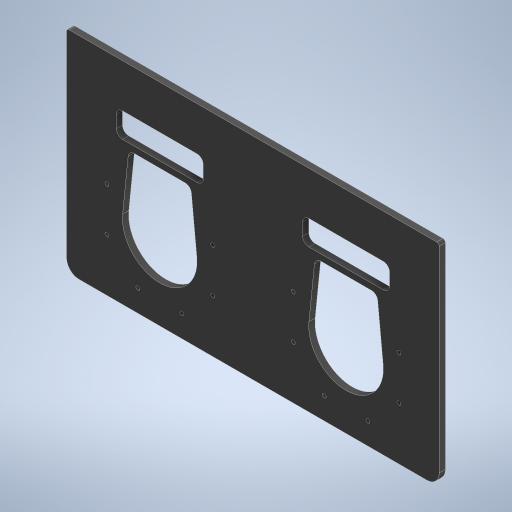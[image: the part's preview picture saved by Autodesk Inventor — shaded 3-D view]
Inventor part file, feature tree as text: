
AUTODESK INVENTOR PART (.ipt)
format: ipt  version: 2024.3 (Build 283343000, 343)  size: 397,824 bytes
history: native  units: mm
features: extrude x5, sketch x5, fillet x3, other x1
ambient origin geometry x8: Origin, YZ Plane, XZ Plane, XY Plane, X Axis, Y Axis, Z Axis, Center Point
bodies: Body1 (feature_tree)
feature tree (14):
  other  "ソリッド1"
  extrude  "押し出し1"  Depth=175.0mm
  extrude  "押し出し2"  Depth=300.0mm
  extrude  "押し出し3"  Depth=5.0mm TaperAngle=0.0deg
  extrude  "押し出し4"  TaperAngle=0.0deg  [1 undecoded]
  fillet  "フィレット2"  [1 undecoded]
  extrude  "押し出し5"  Depth=150.0mm
  fillet  "フィレット6"  Radius=75.0mm
  fillet  "フィレット7"  Radius=5.0mm
  sketch  "スケッチ1"
  sketch  "スケッチ2"
  sketch  "スケッチ3"
  sketch  "スケッチ4"
  sketch  "スケッチ5"
note: 2 required parameter values undecoded (feature->parameter linkage not recoverable at this tier; creation-order binding heuristic only, values carry confidence <= 0.55)
